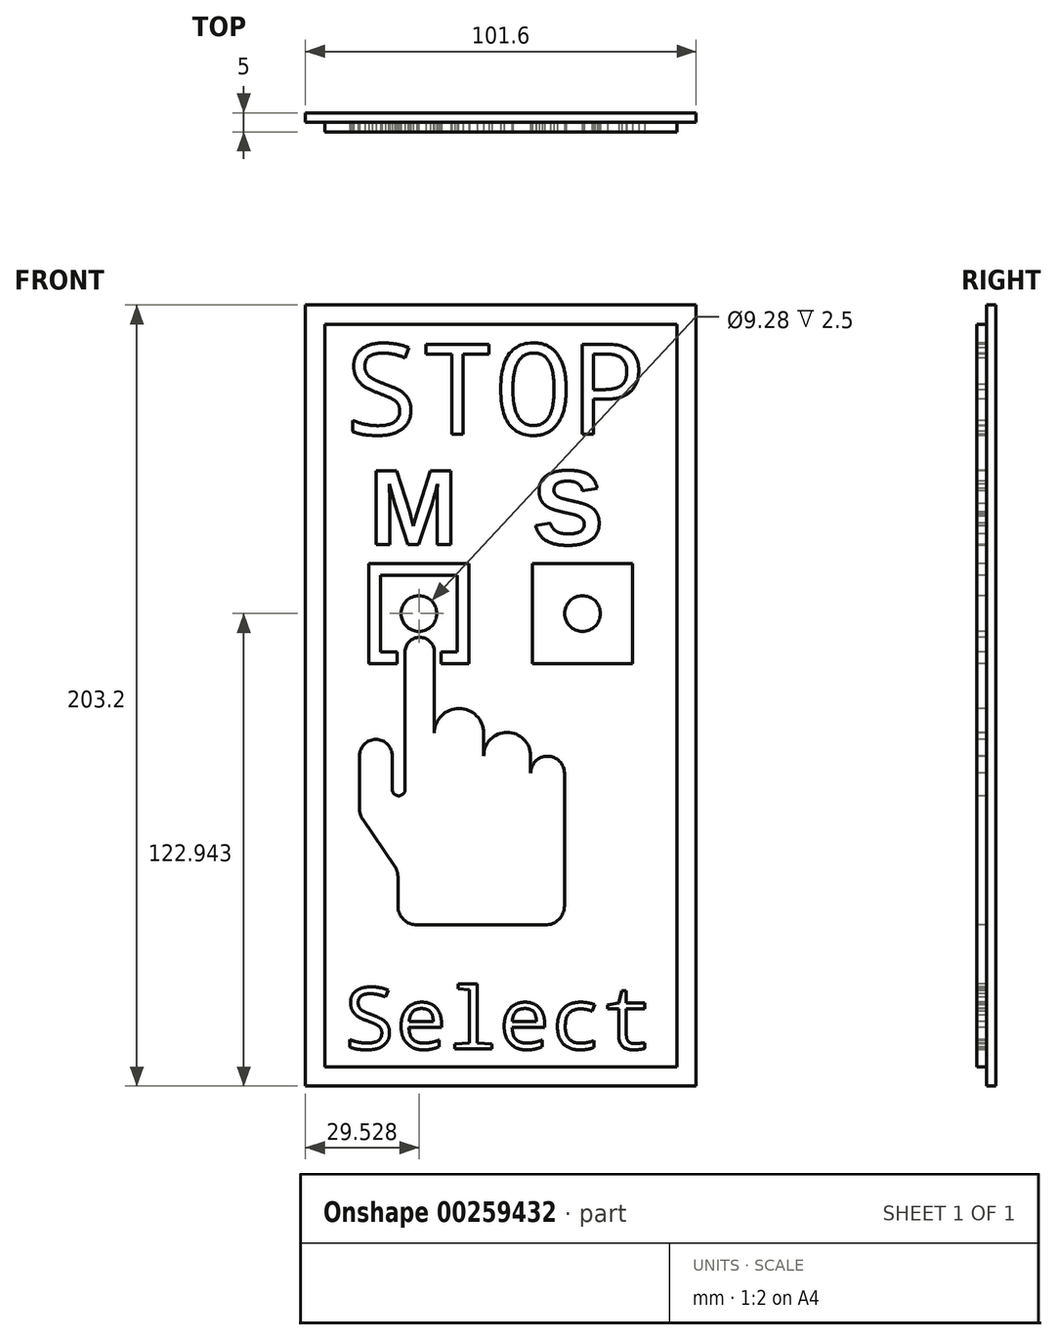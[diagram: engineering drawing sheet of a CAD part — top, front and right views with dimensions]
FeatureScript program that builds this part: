
annotation { "Feature Type Name" : "Feature", "Feature Type Description" : "" }
export const myFeature = defineFeature(function(context is Context, id is Id, definition is map)
    precondition{}
    {
        {
            var Q0;
            Q0=qCreatedBy(makeId("Front.planeOp"),FACE);
            var sketch = newSketch(context, id + "F0", { "sketchPlane" : qUnion([Q0])});
            skLineSegment(sketch, "E0.bottom", {"start": v(0, 0) * mm, "end": v(101.6, 0) * mm});
            skLineSegment(sketch, "E0.top", {"start": v(0, 203.2) * mm, "end": v(101.6, 203.2) * mm});
            skLineSegment(sketch, "E0.left", {"start": v(0, 0) * mm, "end": v(0, 203.2) * mm});
            skLineSegment(sketch, "E0.right", {"start": v(101.6, 0) * mm, "end": v(101.6, 203.2) * mm});
            skLineSegment(sketch, "E1.0", {"start": v(5, 5) * mm, "end": v(5, 198.2) * mm});
            skLineSegment(sketch, "E1.1", {"start": v(5, 5) * mm, "end": v(96.6, 5) * mm});
            skLineSegment(sketch, "E1.2", {"start": v(96.6, 5) * mm, "end": v(96.6, 198.2) * mm});
            skLineSegment(sketch, "E1.3", {"start": v(5, 198.2) * mm, "end": v(96.6, 198.2) * mm});
            skSolve(sketch);
        }
        {
            var Q0;
            Q0=makeQuery(id+"F0.imprint","IMPRINT",FACE,{"disambiguationData":[TD([[makeQuery(id+"F0.imprint","IMPRINT",EDGE,{"derivedFrom":sQuery(id+"F0.wireOp",EDGE,"E1.0")}),-1.0]])]});
            extrude(context, id + "F1", {"entities" : qUnion([Q0]), "depth" : 5 * mm, "offsetDistance" : 25 * mm});
        }
        {
            var Q0;
            Q0=makeQuery(id+"F0.imprint","IMPRINT",FACE,{"disambiguationData":[TD([[makeQuery(id+"F0.imprint","IMPRINT",EDGE,{"derivedFrom":sQuery(id+"F0.wireOp",EDGE,"E0.bottom")}),1.0]])]});
            extrude(context, id + "F2", {"entities" : qUnion([Q0]), "operationType" : NewBodyOperationType.ADD, "depth" : 2.5 * mm, "offsetDistance" : 25 * mm});
        }
        {
            var Q0;
            Q0=makeQuery(id+"F1.opExtrude","CAP_FACE",FACE,{"disambiguationData":[OSD([sQuery(id+"F0.wireOp",EDGE,"E1.0"),sQuery(id+"F0.wireOp",EDGE,"E1.1"),sQuery(id+"F0.wireOp",EDGE,"E1.2"),sQuery(id+"F0.wireOp",EDGE,"E1.3")])],"isStart":false});
            var sketch = newSketch(context, id + "F3", { "sketchPlane" : qUnion([Q0])});
            skLineSegment(sketch, "E2.0", {"start": v(10, 10) * mm, "end": v(10, 193.2) * mm, "construction": true});
            skLineSegment(sketch, "E2.1", {"start": v(10, 10) * mm, "end": v(91.6, 10) * mm, "construction": true});
            skLineSegment(sketch, "E2.2", {"start": v(91.6, 10) * mm, "end": v(91.6, 193.2) * mm, "construction": true});
            skLineSegment(sketch, "E2.3", {"start": v(10, 193.2) * mm, "end": v(91.6, 193.2) * mm, "construction": true});
            skText(sketch, "E3", { "text": "STOP", "fontName": "DroidSansMono.ttf"});
            skLineSegment(sketch, "E4.bottom", {"start": v(19.53, 132.94) * mm, "end": v(39.53, 132.94) * mm});
            skLineSegment(sketch, "E4.top", {"start": v(19.53, 112.94) * mm, "end": v(39.53, 112.94) * mm});
            skLineSegment(sketch, "E4.left", {"start": v(19.53, 132.94) * mm, "end": v(19.53, 112.94) * mm});
            skLineSegment(sketch, "E4.right", {"start": v(39.53, 132.94) * mm, "end": v(39.53, 112.94) * mm});
            skPoint(sketch, "E4.middle", {"position": v(29.53, 122.94) * mm});
            skLineSegment(sketch, "E5.0", {"start": v(16.53, 135.94) * mm, "end": v(42.53, 135.94) * mm});
            skLineSegment(sketch, "E5.1", {"start": v(16.53, 135.94) * mm, "end": v(16.53, 109.94) * mm});
            skLineSegment(sketch, "E5.2", {"start": v(16.53, 109.94) * mm, "end": v(42.53, 109.94) * mm});
            skLineSegment(sketch, "E5.3", {"start": v(42.53, 135.94) * mm, "end": v(42.53, 109.94) * mm});
            skCircle(sketch, "E6", {"center": v(29.53, 122.94) * mm, "radius": 4.64 * mm});
            skLineSegment(sketch, "E7", {"start": v(10, 116.25) * mm, "end": v(10, 95.36) * mm});
            skLineSegment(sketch, "E8", {"start": v(24.06, 54.43) * mm, "end": v(24.06, 46.92) * mm});
            skLineSegment(sketch, "E9", {"start": v(29.06, 41.92) * mm, "end": v(57.08, 41.92) * mm});
            skLineSegment(sketch, "E10", {"start": v(57.08, 41.92) * mm, "end": v(62.35, 41.92) * mm});
            skLineSegment(sketch, "E11", {"start": v(67.35, 46.92) * mm, "end": v(67.35, 81.44) * mm});
            skLineSegment(sketch, "E12", {"start": v(25.91, 112.94) * mm, "end": v(25.91, 77.18) * mm});
            skLineSegment(sketch, "E13", {"start": v(23.19, 57.25) * mm, "end": v(14.93, 69.34) * mm});
            skLineSegment(sketch, "E14", {"start": v(14.06, 72.16) * mm, "end": v(14.06, 85.93) * mm});
            skArc(sketch, "E15", {"start": v(22.59, 85.93) * mm, "mid": v(18.32, 90.2) * mm, "end": v(14.06, 85.93) * mm});
            skLineSegment(sketch, "E16", {"start": v(22.59, 85.93) * mm, "end": v(22.59, 77.18) * mm});
            skArc(sketch, "E17", {"start": v(22.59, 77.18) * mm, "mid": v(24.25, 75.52) * mm, "end": v(25.91, 77.18) * mm});
            skArc(sketch, "E18", {"start": v(33.53, 112.94) * mm, "mid": v(29.72, 116.75) * mm, "end": v(25.91, 112.94) * mm});
            skLineSegment(sketch, "E19", {"start": v(33.53, 112.94) * mm, "end": v(33.53, 91.84) * mm});
            skLineSegment(sketch, "E20", {"start": v(23.9, 112.94) * mm, "end": v(23.9, 109.94) * mm});
            skLineSegment(sketch, "E21", {"start": v(35.28, 112.94) * mm, "end": v(35.28, 109.94) * mm});
            skText(sketch, "E22", { "text": "Select", "fontName": "DroidSansMono.ttf"});
            skLineSegment(sketch, "E23", {"start": v(50.8, 169.55) * mm, "end": v(50.8, 115.43) * mm, "construction": true});
            skCircle(sketch, "E24.MirrorC", {"center": v(72.07, 122.94) * mm, "radius": 4.64 * mm});
            skLineSegment(sketch, "E25.MirrorCS", {"start": v(59.07, 135.94) * mm, "end": v(59.07, 109.94) * mm});
            skLineSegment(sketch, "E26.MirrorCS", {"start": v(85.07, 109.94) * mm, "end": v(59.07, 109.94) * mm});
            skLineSegment(sketch, "E27.MirrorCS", {"start": v(85.07, 135.94) * mm, "end": v(85.07, 109.94) * mm});
            skLineSegment(sketch, "E28.MirrorCS", {"start": v(85.07, 135.94) * mm, "end": v(59.07, 135.94) * mm});
            skLineSegment(sketch, "E29.MirrorCS", {"start": v(62.07, 132.94) * mm, "end": v(62.07, 112.94) * mm});
            skLineSegment(sketch, "E30.MirrorCS", {"start": v(82.07, 132.94) * mm, "end": v(82.07, 112.94) * mm});
            skLineSegment(sketch, "E31.MirrorCS", {"start": v(82.07, 112.94) * mm, "end": v(62.07, 112.94) * mm});
            skLineSegment(sketch, "E32.MirrorCS", {"start": v(82.07, 132.94) * mm, "end": v(62.07, 132.94) * mm});
            skLineSegment(sketch, "E33.0", {"start": v(16.53, 140.94) * mm, "end": v(42.53, 140.94) * mm, "construction": true});
            skLineSegment(sketch, "E34.MirrorCS", {"start": v(85.07, 140.94) * mm, "end": v(59.07, 140.94) * mm, "construction": true});
            skText(sketch, "E35", { "text": "M", "fontName": "Arimo-Bold.ttf"});
            skText(sketch, "E36", { "text": "S", "fontName": "Arimo-Bold.ttf"});
            skPoint(sketch, "E37.visualSharp", {"position": v(14.06, 70.62) * mm});
            skArc(sketch, "E37.filletArc", {"start": v(14.06, 72.16) * mm, "mid": v(14.28, 70.69) * mm, "end": v(14.93, 69.34) * mm});
            skPoint(sketch, "E38.visualSharp", {"position": v(24.06, 55.98) * mm});
            skArc(sketch, "E38.filletArc", {"start": v(24.06, 54.43) * mm, "mid": v(23.84, 55.9) * mm, "end": v(23.19, 57.25) * mm});
            skPoint(sketch, "E39.visualSharp", {"position": v(24.06, 41.92) * mm});
            skArc(sketch, "E39.filletArc", {"start": v(24.06, 46.92) * mm, "mid": v(25.52, 43.39) * mm, "end": v(29.06, 41.92) * mm});
            skPoint(sketch, "E40.visualSharp", {"position": v(67.35, 41.92) * mm});
            skArc(sketch, "E40.filletArc", {"start": v(62.35, 41.92) * mm, "mid": v(65.89, 43.39) * mm, "end": v(67.35, 46.92) * mm});
            skArc(sketch, "E41", {"start": v(46.37, 91.84) * mm, "mid": v(39.95, 98.25) * mm, "end": v(33.53, 91.84) * mm});
            skLineSegment(sketch, "E42", {"start": v(46.37, 91.84) * mm, "end": v(46.37, 85.93) * mm});
            skArc(sketch, "E43", {"start": v(58.56, 85.93) * mm, "mid": v(52.46, 92.03) * mm, "end": v(46.37, 85.93) * mm});
            skLineSegment(sketch, "E44", {"start": v(58.56, 85.93) * mm, "end": v(58.56, 81.44) * mm});
            skArc(sketch, "E45", {"start": v(67.35, 81.44) * mm, "mid": v(62.96, 85.83) * mm, "end": v(58.56, 81.44) * mm});
            const initialGuessF3  = {"E3": [0.01, 0.16955, 1, 0, 0.02365], "E22": [0.01, 0.00965, 1, 0, 0.01609], "E35": [0.01653, 0.14094, 1, 0, 0.01996], "E36": [0.05907, 0.14094, 1, 0, 0.01986]};
            skSetInitialGuess(sketch, initialGuessF3);
            skSolve(sketch);
        }
        {
            var Q0;
            Q0=makeQuery(id+"F3.imprint","IMPRINT",FACE,{"disambiguationData":[TD([[makeQuery(id+"F3.imprint","IMPRINT",EDGE,{"derivedFrom":sQuery(id+"F3.wireOp",EDGE,"E3.sketch_text.stroke-0")}),-1.0]])]});
            var Q1;
            Q1=makeQuery(id+"F3.imprint","IMPRINT",FACE,{"disambiguationData":[TD([[makeQuery(id+"F3.imprint","IMPRINT",EDGE,{"derivedFrom":sQuery(id+"F3.wireOp",EDGE,"E3.sketch_text.stroke-20")}),-1.0]])]});
            var Q2;
            Q2=makeQuery(id+"F3.imprint","IMPRINT",FACE,{"disambiguationData":[TD([[makeQuery(id+"F3.imprint","IMPRINT",EDGE,{"derivedFrom":sQuery(id+"F3.wireOp",EDGE,"E22.sketch_text.stroke-0")}),-1.0]])]});
            var Q3;
            Q3=makeQuery(id+"F3.imprint","IMPRINT",FACE,{"disambiguationData":[TD([[makeQuery(id+"F3.imprint","IMPRINT",EDGE,{"derivedFrom":sQuery(id+"F3.wireOp",EDGE,"E22.sketch_text.stroke-35")}),-1.0]])]});
            var Q4;
            Q4=makeQuery(id+"F3.imprint","IMPRINT",FACE,{"disambiguationData":[TD([[makeQuery(id+"F3.imprint","IMPRINT",EDGE,{"derivedFrom":sQuery(id+"F3.wireOp",EDGE,"E22.sketch_text.stroke-60")}),-1.0]])]});
            var Q5;
            Q5=makeQuery(id+"F3.imprint","IMPRINT",FACE,{"disambiguationData":[TD([[makeQuery(id+"F3.imprint","IMPRINT",EDGE,{"derivedFrom":sQuery(id+"F3.wireOp",EDGE,"E22.sketch_text.stroke-72")}),-1.0]])]});
            var Q6;
            Q6=makeQuery(id+"F3.imprint","IMPRINT",FACE,{"disambiguationData":[TD([[makeQuery(id+"F3.imprint","IMPRINT",EDGE,{"derivedFrom":sQuery(id+"F3.wireOp",EDGE,"E3.sketch_text.stroke-28")}),-1.0]])]});
            var Q7;
            Q7=makeQuery(id+"F3.imprint","IMPRINT",FACE,{"disambiguationData":[TD([[makeQuery(id+"F3.imprint","IMPRINT",EDGE,{"derivedFrom":sQuery(id+"F3.wireOp",EDGE,"E3.sketch_text.stroke-40")}),-1.0]])]});
            var Q8;
            Q8=makeQuery(id+"F3.imprint","IMPRINT",FACE,{"disambiguationData":[TD([[makeQuery(id+"F3.imprint","IMPRINT",EDGE,{"derivedFrom":sQuery(id+"F3.wireOp",EDGE,"E8")}),1.0]])]});
            var Q9;
            Q9=makeQuery(id+"F3.imprint","IMPRINT",FACE,{"disambiguationData":[TD([[makeQuery(id+"F3.imprint","IMPRINT",EDGE,{"derivedFrom":sQuery(id+"F3.wireOp",EDGE,"E22.sketch_text.stroke-20")}),-1.0]])]});
            var Q10;
            Q10=makeQuery(id+"F3.imprint","IMPRINT",FACE,{"disambiguationData":[TD([[makeQuery(id+"F3.imprint","IMPRINT",EDGE,{"derivedFrom":sQuery(id+"F3.wireOp",EDGE,"E22.sketch_text.stroke-45")}),-1.0]])]});
            var Q11;
            Q11=makeQuery(id+"F3.imprint","IMPRINT",FACE,{"disambiguationData":[TD([[makeQuery(id+"F3.imprint","IMPRINT",EDGE,{"derivedFrom":sQuery(id+"F3.wireOp",EDGE,"E4.bottom")}),1.0]])]});
            var Q12;
            {var subQ1=sQuery(id+"F3.wireOp",EDGE,"E12");var subQ6=sQuery(id+"F3.wireOp",EDGE,"E5.2");var subQ7=makeQuery(id+"F3.imprint","INTERSECT",VERTEX,{"derivedFrom":[subQ6,subQ1]});Q12=makeQuery(id+"F3.imprint","IMPRINT",FACE,{"disambiguationData":[TD([[makeQuery(id+"F3.imprint","IMPRINT",EDGE,{"disambiguationData":[TD([[subQ7,-1.0]])],"derivedFrom":subQ6}),1.0]])]});}
            var Q13;
            Q13=makeQuery(id+"F3.imprint","IMPRINT",FACE,{"disambiguationData":[TD([[makeQuery(id+"F3.imprint","IMPRINT",EDGE,{"derivedFrom":sQuery(id+"F3.wireOp",EDGE,"E6")}),1.0]])]});
            var Q14;
            {var subQ0=sQuery(id+"F3.wireOp",EDGE,"E18");Q14=makeQuery(id+"F3.imprint","IMPRINT",FACE,{"disambiguationData":[TD([[makeQuery(id+"F3.imprint","IMPRINT",EDGE,{"derivedFrom":subQ0}),1.0]])]});}
            var Q15;
            Q15=makeQuery(id+"F3.imprint","IMPRINT",FACE,{"disambiguationData":[TD([[makeQuery(id+"F3.imprint","IMPRINT",EDGE,{"derivedFrom":sQuery(id+"F3.wireOp",EDGE,"E25.MirrorCS")}),1.0]])]});
            var Q16;
            Q16=makeQuery(id+"F3.imprint","IMPRINT",FACE,{"disambiguationData":[TD([[makeQuery(id+"F3.imprint","IMPRINT",EDGE,{"derivedFrom":sQuery(id+"F3.wireOp",EDGE,"E24.MirrorC")}),-1.0]])]});
            var Q17;
            Q17=makeQuery(id+"F3.imprint","IMPRINT",FACE,{"disambiguationData":[TD([[makeQuery(id+"F3.imprint","IMPRINT",EDGE,{"derivedFrom":sQuery(id+"F3.wireOp",EDGE,"E35.sketch_text.stroke-0")}),-1.0]])]});
            var Q18;
            Q18=makeQuery(id+"F3.imprint","IMPRINT",FACE,{"disambiguationData":[TD([[makeQuery(id+"F3.imprint","IMPRINT",EDGE,{"derivedFrom":sQuery(id+"F3.wireOp",EDGE,"E36.sketch_text.stroke-0")}),-1.0]])]});
            extrude(context, id + "F4", {"entities" : qUnion([Q0, Q1, Q2, Q3, Q4, Q5, Q6, Q7, Q8, Q9, Q10, Q11, Q12, Q13, Q14, Q15, Q16, Q17, Q18]), "operationType" : NewBodyOperationType.REMOVE, "oppositeDirection" : true, "depth" : 2.5 * mm, "offsetDistance" : 25 * mm});
        }
    });
